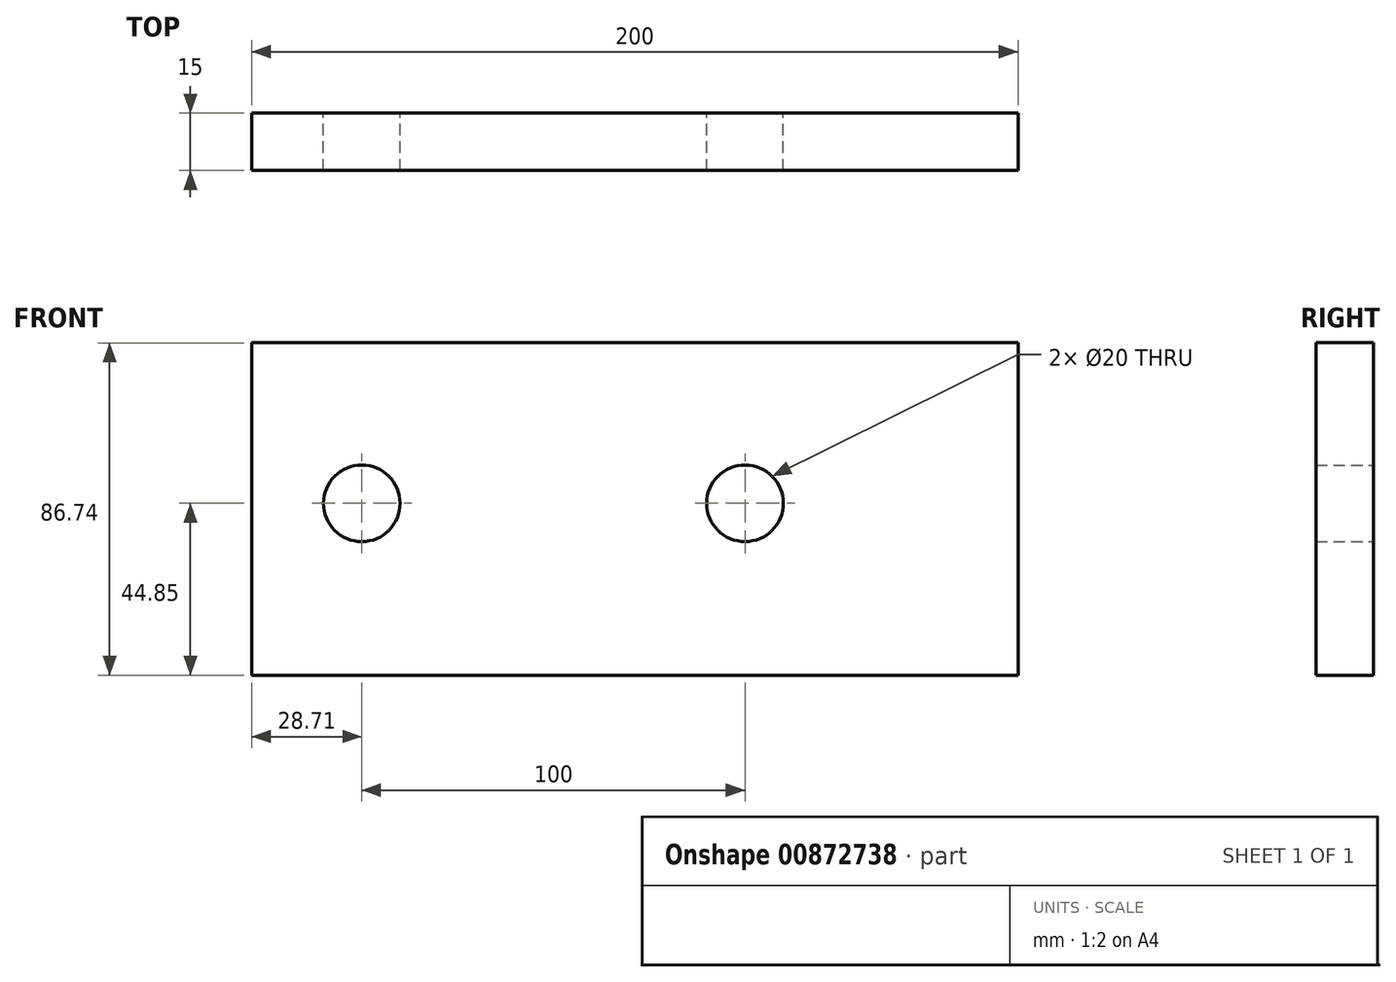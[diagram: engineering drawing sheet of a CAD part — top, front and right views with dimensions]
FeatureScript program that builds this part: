
annotation { "Feature Type Name" : "Feature", "Feature Type Description" : "" }
export const myFeature = defineFeature(function(context is Context, id is Id, definition is map)
    precondition{}
    {
        {
            var Q0;
            Q0=qCreatedBy(makeId("Front.planeOp"),FACE);
            var sketch = newSketch(context, id + "F0", { "sketchPlane" : qUnion([Q0])});
            skLineSegment(sketch, "E0.bottom", {"start": v(-28.71, 41.9) * mm, "end": v(171.29, 41.9) * mm});
            skLineSegment(sketch, "E0.top", {"start": v(-28.71, -44.85) * mm, "end": v(171.29, -44.85) * mm});
            skLineSegment(sketch, "E0.left", {"start": v(-28.71, 41.9) * mm, "end": v(-28.71, -44.85) * mm});
            skLineSegment(sketch, "E0.right", {"start": v(171.29, 41.9) * mm, "end": v(171.29, -44.85) * mm});
            skCircle(sketch, "E1", {"center": v(0, 0) * mm, "radius": 10 * mm});
            skCircle(sketch, "E2", {"center": v(100, 0) * mm, "radius": 10 * mm});
            skSolve(sketch);
        }
        {
            var Q0;
            Q0=makeQuery(id+"F0.imprint","IMPRINT",FACE,{"disambiguationData":[TD([[makeQuery(id+"F0.imprint","IMPRINT",EDGE,{"derivedFrom":sQuery(id+"F0.wireOp",EDGE,"E0.bottom")}),-1.0]])]});
            extrude(context, id + "F1", {"entities" : qUnion([Q0]), "depth" : 15 * mm, "offsetDistance" : 25 * mm});
        }
    });
